FCSTD DOCUMENT
Label: PR_005_pontosítandó
objects: Sketcher::SketchObject×1
note: 1 computed .brp shape members not serialized (recipe doc carries the construction recipe); baked Part::Feature solids carry a one-line shape summary decoded from their .brp

FEATURE [Sketcher::SketchObject] Sketch
  sketch-geometry (6):
    g0: LineSegment [constr] StartX=-98.0998 StartY=-954.92 StartZ=0 EndX=250 EndY=-954.92 EndZ=0
    g1: LineSegment [constr] StartX=250 StartY=-954.92 StartZ=0 EndX=250 EndY=-1054.92 EndZ=0
    g2: LineSegment [constr] StartX=250 StartY=-1054.92 StartZ=0 EndX=-117.743 EndY=-1054.92 EndZ=0
    g3: ArcOfCircle CenterX=38 CenterY=-992.92 CenterZ=0 NormalX=0 NormalY=0 NormalZ=1 Radius=38 StartAngle=1.5708 EndAngle=5.14629
    g4: LineSegment StartX=38 StartY=-954.92 StartZ=0 EndX=88 EndY=-954.92 EndZ=0
    g5: ArcOfCircle CenterX=225 CenterY=-993.816 CenterZ=0 NormalX=0 NormalY=0 NormalZ=1 Radius=25 StartAngle=6.28319 EndAngle=7.38615
  constraints (16):
    c: Horizontal(g0)
    c: DistanceY(g-1,g0) = -954.92
    c: Vertical(g1)
    c: Horizontal(g2)
    c: Coincident(g2,g1)
    c: Coincident(g0,g1)
    c: Distance(g1) = 100
    c: DistanceX(g1) = 250
    c: Radius(g3) = 38
    c: Tangent(g3,g-2)
    c: Horizontal(g4)
    c: Tangent(g3,g0)
    c: Distance(g4) = 50
    c: Coincident(g3,g4)
    c: Radius(g5) = 25
    c: Tangent(g5,g1)
